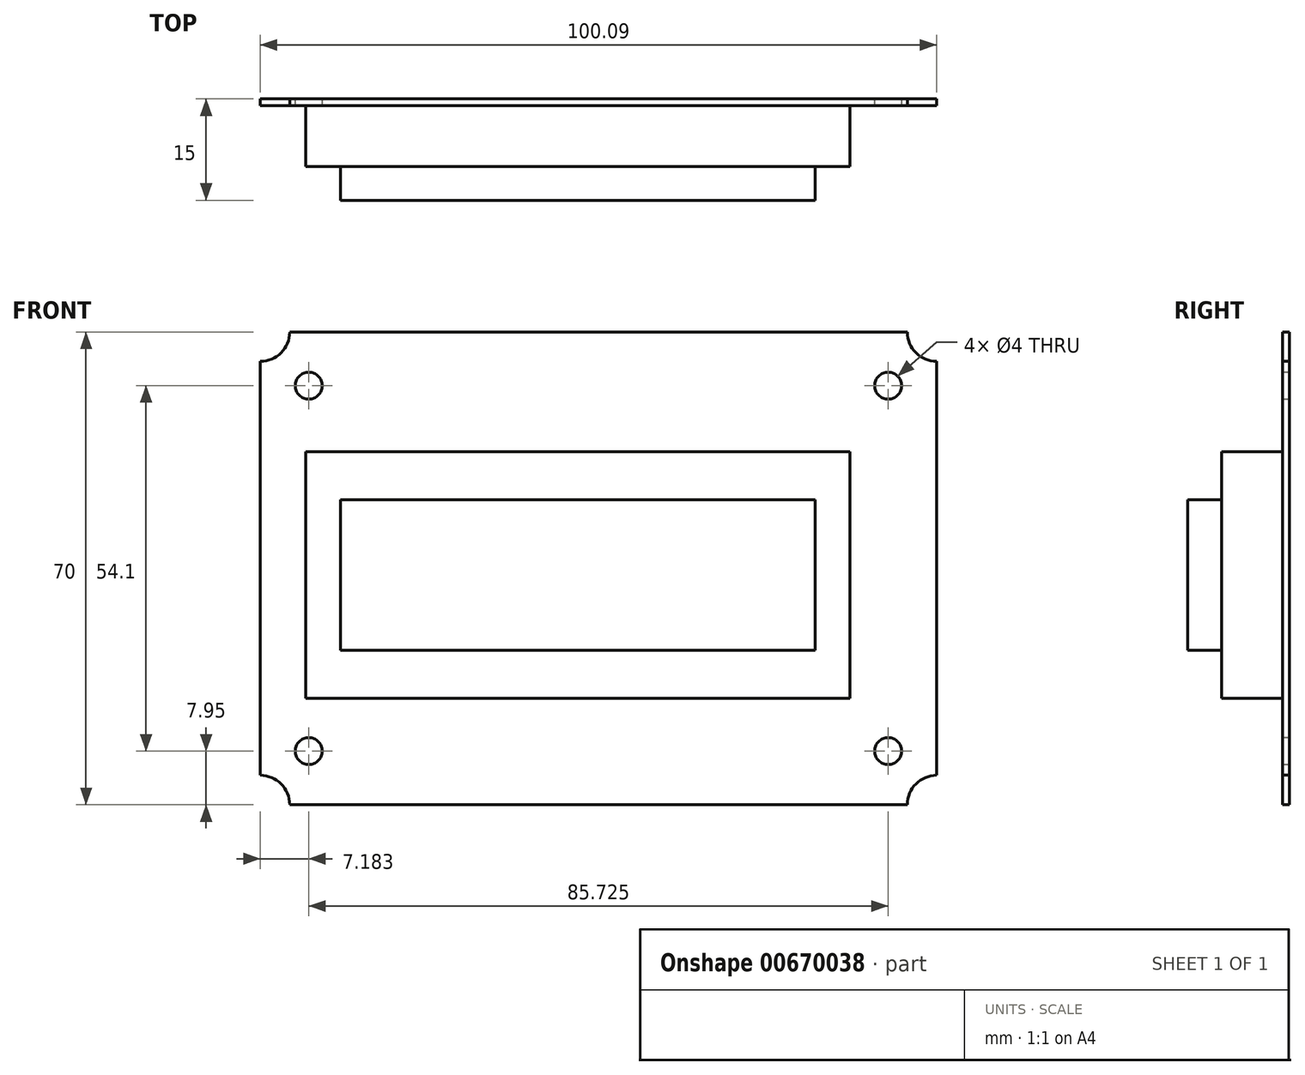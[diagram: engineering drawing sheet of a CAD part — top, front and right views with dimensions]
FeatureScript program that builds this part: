
annotation { "Feature Type Name" : "Feature", "Feature Type Description" : "" }
export const myFeature = defineFeature(function(context is Context, id is Id, definition is map)
    precondition{}
    {
        {
            var Q0;
            Q0=qCreatedBy(makeId("Front.planeOp"),FACE);
            var sketch = newSketch(context, id + "F0", { "sketchPlane" : qUnion([Q0])});
            skCircle(sketch, "E0", {"center": v(7.18, 7.95) * mm, "radius": 2 * mm});
            skCircle(sketch, "E1", {"center": v(7.18, 62.05) * mm, "radius": 2 * mm});
            skLineSegment(sketch, "E2", {"start": v(0, 35) * mm, "end": v(100.1, 35) * mm, "construction": true});
            skLineSegment(sketch, "E3", {"start": v(50.05, 70) * mm, "end": v(50.05, 0) * mm, "construction": true});
            skCircle(sketch, "E4", {"center": v(92.9, 62.05) * mm, "radius": 2 * mm});
            skCircle(sketch, "E5", {"center": v(92.9, 7.95) * mm, "radius": 2 * mm});
            skArc(sketch, "E6", {"start": v(0, 65.64) * mm, "mid": v(3.08, 66.92) * mm, "end": v(4.36, 70) * mm});
            skArc(sketch, "E7", {"start": v(95.73, 70) * mm, "mid": v(97, 66.92) * mm, "end": v(100.1, 65.64) * mm});
            skArc(sketch, "E8", {"start": v(100.1, 4.36) * mm, "mid": v(97, 3.08) * mm, "end": v(95.73, 0) * mm});
            skArc(sketch, "E9", {"start": v(4.36, 0) * mm, "mid": v(3.08, 3.08) * mm, "end": v(0, 4.36) * mm});
            skLineSegment(sketch, "E10", {"start": v(4.36, 70) * mm, "end": v(95.73, 70) * mm});
            skLineSegment(sketch, "E11", {"start": v(100.1, 65.64) * mm, "end": v(100.1, 4.36) * mm});
            skLineSegment(sketch, "E12", {"start": v(95.73, 0) * mm, "end": v(4.36, 0) * mm});
            skLineSegment(sketch, "E13", {"start": v(0, 65.64) * mm, "end": v(0, 4.36) * mm});
            skLineSegment(sketch, "E14.bottom", {"start": v(6.75, 52.26) * mm, "end": v(87.25, 52.26) * mm});
            skLineSegment(sketch, "E14.top", {"start": v(6.75, 15.74) * mm, "end": v(87.25, 15.74) * mm});
            skLineSegment(sketch, "E14.left", {"start": v(6.75, 52.26) * mm, "end": v(6.75, 15.74) * mm});
            skLineSegment(sketch, "E14.right", {"start": v(87.25, 52.26) * mm, "end": v(87.25, 15.74) * mm});
            skLineSegment(sketch, "E15", {"start": v(47, 52.26) * mm, "end": v(47, 15.74) * mm, "construction": true});
            skLineSegment(sketch, "E16", {"start": v(6.75, 34) * mm, "end": v(87.25, 34) * mm, "construction": true});
            skPoint(sketch, "E17", {"position": v(47, 34) * mm});
            skLineSegment(sketch, "E18.bottom", {"start": v(11.88, 45.14) * mm, "end": v(82.12, 45.14) * mm});
            skLineSegment(sketch, "E18.top", {"start": v(11.88, 22.86) * mm, "end": v(82.12, 22.86) * mm});
            skLineSegment(sketch, "E18.left", {"start": v(11.88, 45.14) * mm, "end": v(11.88, 22.86) * mm});
            skLineSegment(sketch, "E18.right", {"start": v(82.12, 45.14) * mm, "end": v(82.12, 22.86) * mm});
            skPoint(sketch, "E19", {"position": v(50.05, 35) * mm});
            skSolve(sketch);
        }
        {
            var Q0;
            Q0=makeQuery(id+"F0.imprint","IMPRINT",FACE,{"disambiguationData":[TD([[makeQuery(id+"F0.imprint","IMPRINT",EDGE,{"derivedFrom":sQuery(id+"F0.wireOp",EDGE,"E0")}),-1.0]])]});
            extrude(context, id + "F1", {"entities" : qUnion([Q0]), "depth" : 1 * mm, "offsetDistance" : 25 * mm});
        }
        {
            var Q0;
            Q0=makeQuery(id+"F0.imprint","IMPRINT",FACE,{"disambiguationData":[TD([[makeQuery(id+"F0.imprint","IMPRINT",EDGE,{"derivedFrom":sQuery(id+"F0.wireOp",EDGE,"E14.bottom")}),-1.0]])]});
            extrude(context, id + "F2", {"entities" : qUnion([Q0]), "operationType" : NewBodyOperationType.ADD, "depth" : 10 * mm, "offsetDistance" : 25 * mm});
        }
        {
            var Q0;
            Q0=makeQuery(id+"F0.imprint","IMPRINT",FACE,{"disambiguationData":[TD([[makeQuery(id+"F0.imprint","IMPRINT",EDGE,{"derivedFrom":sQuery(id+"F0.wireOp",EDGE,"E18.bottom")}),-1.0]])]});
            extrude(context, id + "F3", {"entities" : qUnion([Q0]), "operationType" : NewBodyOperationType.ADD, "depth" : 15 * mm, "offsetDistance" : 25 * mm});
        }
    });
